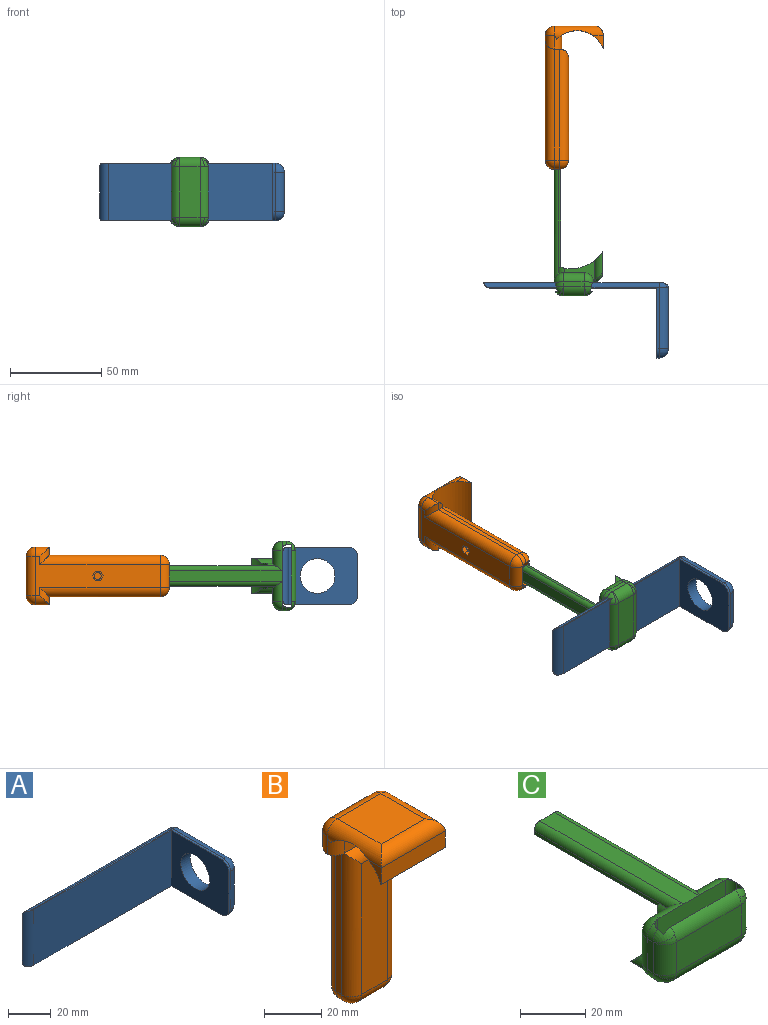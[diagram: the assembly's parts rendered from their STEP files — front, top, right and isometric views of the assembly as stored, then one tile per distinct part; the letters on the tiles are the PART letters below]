
ASSEMBLY  parts=3 mates=2
PART A: 23 faces, bbox 101.6x41.6x32.6 mm
  f0: cylinder r=3.17mm len=24.95mm, axis (0,0,1), area 116.1mm2, adj f1,f5,f12,f14
  f1: plane 98.43x26.67mm, normal (0,1,0), area 2624mm2, adj f0,f9,f10,f13,f16,f22
  f2: plane 94.27x33.66mm, normal (0,0,1), area 101.3mm2, adj f6,f7,f10,f15,f17,f22
  f3: plane 94.27x33.66mm, normal (0,0,-1), area 101.3mm2, adj f6,f7,f9,f11,f21,f22
  f4: plane 21.59x1.27mm, normal (0,-1,0), area 27.4mm2, adj f7,f17,f19,f21
  f5: plane 33.02x21.59mm, normal (1,0,0), area 427.9mm2, adj f0,f8,f11,f15,f19
  f6: plane 90.54x31.75mm, normal (0,-1,0), area 2874.7mm2, adj f2,f3,f7,f22
  f7: plane 38.1x31.75mm, normal (-1,0,0), area 913.6mm2, adj f2,f3,f4,f6,f8,f17,f21
  f8: cylinder r=9.53mm len=19.05mm, axis (1,0,0), area 380mm2, adj f5,f7
  f9: cylinder r=2.54mm len=96.52mm, axis (-1,0,0), area 382.7mm2, adj f1,f3,f13,f22
  f10: cylinder r=2.54mm len=96.52mm, axis (-1,0,0), area 382.7mm2, adj f1,f2,f16,f22
  f11: cylinder r=5.08mm len=33.66mm, axis (0,1,0), area 267.4mm2, adj f3,f5,f12,f13,f20
  f12: bspline ~4x3.91mm, area 8.6mm2, adj f0,f11,f13
  f13: torus R=2.54mm, axis (0,-1,0), area 14.1mm2, adj f1,f9,f11,f12
  f14: bspline ~4x3.91mm, area 8.6mm2, adj f0,f15,f16
  f15: cylinder r=5.08mm len=33.66mm, axis (0,-1,0), area 267.4mm2, adj f2,f5,f14,f16,f18
  f16: torus R=2.54mm, axis (0,-1,0), area 14.1mm2, adj f1,f10,f14,f15
  f17: cylinder r=5.08mm len=5.08mm, axis (-1,0,0), area 10.1mm2, adj f2,f4,f7,f18
  f18: sphere r=5.08mm, area 40.5mm2, adj f15,f17,f19
  f19: cylinder r=5.08mm len=21.59mm, axis (0,0,-1), area 172.3mm2, adj f4,f5,f18,f20
  f20: sphere r=5.08mm, area 40.5mm2, adj f11,f19,f21
  f21: cylinder r=5.08mm len=5.08mm, axis (1,0,0), area 10.1mm2, adj f3,f4,f7,f20
  f22: cylinder r=5.08mm len=31.75mm, axis (0,0,1), area 188.1mm2, adj f1,f2,f3,f6,f9,f10
PART B: 53 faces, bbox 32.4x32.5x79.4 mm
  f0: plane 7.11x5.98mm, normal (-1,0,0), area 17.6mm2, adj f14,f15,f17,f37
  f1: plane 7.11x5.98mm, normal (1,0,0), area 17.6mm2, adj f14,f15,f17,f40
  f2: plane 68.58x21.59mm, normal (0,1,0), area 874.6mm2, adj f20,f21,f22,f23,f24,f25,f28,f29
  f3: plane 60.96x2.59mm, normal (-1,0,0), area 157.9mm2, adj f18,f29,f31,f47
  f4: plane 56.04x12.75mm, normal (0,-1,0), area 714.6mm2, adj f30,f31,f32,f43
  f5: cylinder r=2.54mm len=63.49mm, axis (0,0,-1), area 253.1mm2, adj f6,f10,f12,f47,f49,f50
  f6: plane 63.46x10.16mm, normal (0,-1,0), area 633.4mm2, adj f5,f7,f12,f27,f50
  f7: cylinder r=2.54mm len=63.49mm, axis (0,0,-1), area 253.1mm2, adj f6,f8,f12,f46,f48,f50
  f8: plane 63.35x2.54mm, normal (-1,0,0), area 160.7mm2, adj f7,f9,f12,f44,f46
  f9: plane 63.38x15.47mm, normal (0,1,0), area 962.3mm2, adj f8,f10,f12,f43,f44,f45
  f10: plane 64x3.2mm, normal (1,0,0), area 160.7mm2, adj f5,f9,f12,f45,f47
  f11: plane 60.96x2.59mm, normal (1,0,0), area 157.9mm2, adj f19,f28,f32,f46
  f12: plane 15.24x5.08mm, normal (0,0,-1), area 74.7mm2, adj f5,f6,f7,f8,f9,f10
  f13: plane 21.69x21.59mm, normal (0,0,1), area 468.3mm2, adj f35,f37,f39,f40
  f14: plane 31.75x7.11mm, normal (0,-1,0), area 225.8mm2, adj f0,f1,f17,f39
  f15: cylinder r=15.35mm len=31.75mm, axis (-1,0,0), area 866.3mm2, adj f0,f1,f16,f17,f37,f40,f41,f42
  f16: plane 21.89x7.62mm, normal (0,-1,0), area 166.8mm2, adj f15,f30,f41,f42
  f17: plane 31.75x0.19mm, normal (0,0,-1), area 6.1mm2, adj f0,f1,f14,f15
  f18: plane 4.58x3.85mm, normal (0,0,-1), area 12.2mm2, adj f3,f31,f42,f51
  f19: plane 4.58x3.85mm, normal (0,0,-1), area 12.2mm2, adj f11,f32,f41,f52
  f20: plane 2.93x2.54mm, normal (1,0,0), area 7.4mm2, adj f2,f21,f25,f26
  f21: plane 2.54x2.54mm, normal (0.5,0,-0.87), area 7.4mm2, adj f2,f20,f22,f26
  f22: plane 2.54x2.54mm, normal (-0.5,0,-0.87), area 7.4mm2, adj f2,f21,f23,f26
  f23: plane 2.93x2.54mm, normal (-1,0,0), area 7.4mm2, adj f2,f22,f24,f26
  f24: plane 2.54x2.54mm, normal (-0.5,0,0.87), area 7.4mm2, adj f2,f23,f25,f26
  f25: plane 2.54x2.54mm, normal (0.5,0,0.87), area 7.4mm2, adj f2,f20,f24,f26
  f26: plane 5.87x5.08mm, normal (0,1,0), area 10.9mm2, adj f20,f21,f22,f23,f24,f25,f27
  f27: cylinder r=1.91mm len=3.81mm, axis (0,1,0), area 22.8mm2, adj f6,f26
  f28: cylinder r=5.08mm len=66.04mm, axis (0,0,-1), area 501.2mm2, adj f2,f11,f48,f52
  f29: cylinder r=5.08mm len=66.04mm, axis (0,0,-1), area 501.2mm2, adj f2,f3,f49,f51
  f30: cylinder r=5.08mm len=22.59mm, axis (-1,0,0), area 124.1mm2, adj f4,f16,f31,f32,f41,f42
  f31: cylinder r=5.08mm len=60.96mm, axis (0,0,-1), area 472.9mm2, adj f3,f4,f18,f30,f42,f45
  f32: cylinder r=5.08mm len=60.96mm, axis (0,0,-1), area 472.9mm2, adj f4,f11,f19,f30,f41,f44
  f33: cylinder r=5.08mm len=7.62mm, axis (0,0,-1), area 46.1mm2, adj f2,f34,f42,f51
  f34: sphere r=5.08mm, area 40.5mm2, adj f33,f35,f37
  f35: cylinder r=5.08mm len=21.59mm, axis (-1,0,0), area 172.3mm2, adj f2,f13,f34,f38
  f36: cylinder r=5.08mm len=7.62mm, axis (0,0,-1), area 46.1mm2, adj f2,f38,f41,f52
  f37: cylinder r=5.08mm len=26.77mm, axis (0,-1,0), area 172.8mm2, adj f0,f13,f15,f34,f39,f42
  f38: sphere r=5.08mm, area 40.5mm2, adj f35,f36,f40
  f39: cylinder r=5.08mm len=31.75mm, axis (-1,0,0), area 223.9mm2, adj f13,f14,f37,f40
  f40: cylinder r=5.08mm len=26.77mm, axis (0,-1,0), area 172.8mm2, adj f1,f13,f15,f38,f39,f41
  f41: cylinder r=5.08mm len=7.62mm, axis (0,0,-1), area 45.9mm2, adj f15,f16,f19,f30,f32,f36,f40
  f42: cylinder r=5.08mm len=7.62mm, axis (0,0,-1), area 45.9mm2, adj f15,f16,f18,f30,f31,f33,f37
  f43: cylinder r=5.08mm len=12.75mm, axis (1,0,0), area 77.5mm2, adj f4,f9,f44,f45
  f44: sphere r=5.08mm, area 38.1mm2, adj f8,f9,f32,f43,f46
  f45: sphere r=5.08mm, area 37.7mm2, adj f9,f10,f31,f43,f47
  f46: cylinder r=5.08mm len=5.07mm, axis (0,-1,0), area 18.2mm2, adj f7,f8,f11,f44,f48
  f47: cylinder r=5.08mm len=5.07mm, axis (0,-1,0), area 18.2mm2, adj f3,f5,f10,f45,f49
  f48: sphere r=5.08mm, area 40.4mm2, adj f7,f28,f46,f50
  f49: sphere r=5.08mm, area 40.4mm2, adj f5,f29,f47,f50
  f50: cylinder r=5.08mm len=12.75mm, axis (1,0,0), area 94.1mm2, adj f2,f5,f6,f7,f48,f49
  f51: cylinder r=5.08mm len=9.5mm, axis (-1,0,0), area 35.3mm2, adj f2,f18,f29,f33
  f52: cylinder r=5.08mm len=9.5mm, axis (-1,0,0), area 35.3mm2, adj f2,f19,f28,f36
PART C: 76 faces, bbox 38.2x70x26.8 mm
  f0: plane 16.33x11.11mm, normal (-1,0,0), area 63.2mm2, adj f1,f2,f9,f66,f69,f73,f74
  f1: cylinder r=13.73mm len=13.97mm, axis (1,0,0), area 54.9mm2, adj f0,f26,f48,f49,f50,f66,f74,f75
  f2: plane 11.43x7.05mm, normal (0,1,0), area 57.1mm2, adj f0,f9,f10,f42,f51,f55,f56,f74
  f3: plane 11.43x7.05mm, normal (0,1,0), area 57.1mm2, adj f6,f7,f12,f49,f61,f62,f63,f75
  f4: cylinder r=2.54mm len=5.08mm, axis (0,1,0), area 40.5mm2, adj f21,f57
  f5: cylinder r=2.54mm len=5.08mm, axis (0,1,0), area 40.5mm2, adj f21,f64
  f6: cylinder r=5.08mm len=11.43mm, axis (0,0,-1), area 88.4mm2, adj f3,f8,f18,f36,f58,f63
  f7: cylinder r=5.08mm len=9.53mm, axis (1,0,0), area 40.3mm2, adj f3,f8,f21,f49,f59,f60,f61,f71
  f8: sphere r=5.08mm, area 38.9mm2, adj f6,f7,f21,f37,f58,f59
  f9: cylinder r=5.08mm len=9.53mm, axis (1,0,0), area 40.3mm2, adj f0,f2,f11,f21,f51,f52,f53,f73
  f10: cylinder r=5.08mm len=11.43mm, axis (0,0,1), area 88.4mm2, adj f2,f11,f17,f44,f54,f55
  f11: sphere r=5.08mm, area 38.9mm2, adj f9,f10,f21,f45,f53,f54
  f12: cylinder r=5.08mm len=10.8mm, axis (1,0,0), area 69mm2, adj f3,f21,f27,f36,f75
  f13: plane 54.1x1.27mm, normal (1,0,0), area 68.7mm2, adj f16,f26,f27,f48
  f14: plane 62.23x6.35mm, normal (0,0,1), area 395.2mm2, adj f16,f21,f27,f28
  f15: plane 54.1x1.27mm, normal (-1,0,0), area 68.7mm2, adj f16,f26,f28,f50
  f16: plane 11.43x3.81mm, normal (0,1,0), area 40.8mm2, adj f13,f14,f15,f26,f27,f28
  f17: plane 11.43x2.54mm, normal (-1,0,0), area 29mm2, adj f10,f31,f43,f45
  f18: plane 11.43x2.54mm, normal (1,0,0), area 29mm2, adj f6,f30,f35,f37
  f19: plane 19.36x2.54mm, normal (-1,0,0), area 47.7mm2, adj f20,f24,f34,f39
  f20: cylinder r=2.54mm len=21.51mm, axis (0,0,1), area 81.3mm2, adj f19,f21,f35,f37
  f21: plane 29.21x21.59mm, normal (0,-1,0), area 590.1mm2, adj f4,f5,f7,f8,f9,f11,f12,f14
  f22: cylinder r=2.54mm len=21.51mm, axis (0,0,1), area 81.3mm2, adj f21,f23,f43,f45
  f23: plane 19.36x2.54mm, normal (1,0,0), area 47.7mm2, adj f22,f24,f41,f46
  f24: plane 34.29x20.23mm, normal (0,1,0), area 688.3mm2, adj f19,f23,f29,f32,f34,f39,f41,f46
  f25: plane 27.94x11.43mm, normal (0,-1,0), area 319.4mm2, adj f29,f30,f31,f32
  f26: plane 54.1x11.43mm, normal (0,0,-1), area 618.3mm2, adj f1,f13,f15,f16
  f27: cylinder r=2.54mm len=62.23mm, axis (0,1,0), area 238.3mm2, adj f12,f13,f14,f16,f75
  f28: cylinder r=2.54mm len=62.23mm, axis (0,1,0), area 238.3mm2, adj f14,f15,f16,f42,f74
  f29: cylinder r=5.08mm len=27.94mm, axis (-1,0,0), area 148.6mm2, adj f24,f25,f33,f34,f40,f41
  f30: cylinder r=5.08mm len=11.43mm, axis (0,0,-1), area 91.2mm2, adj f18,f25,f33,f38
  f31: cylinder r=5.08mm len=11.43mm, axis (0,0,-1), area 91.2mm2, adj f17,f25,f40,f47
  f32: cylinder r=5.08mm len=27.94mm, axis (-1,0,0), area 148.6mm2, adj f24,f25,f38,f39,f46,f47
  f33: sphere r=5.08mm, area 10.4mm2, adj f29,f30,f34
  f34: sphere r=5.08mm, area 20.9mm2, adj f19,f24,f29,f33,f35
  f35: cylinder r=5.08mm len=5.04mm, axis (0,-1,0), area 13.2mm2, adj f18,f20,f34,f36
  f36: sphere r=5.08mm, area 40.5mm2, adj f6,f12,f21,f35
  f37: cylinder r=5.08mm len=5.04mm, axis (0,-1,0), area 13.2mm2, adj f8,f18,f20,f39
  f38: sphere r=5.08mm, area 10.4mm2, adj f30,f32,f39
  f39: sphere r=5.08mm, area 20.9mm2, adj f19,f24,f32,f37,f38
  f40: sphere r=5.08mm, area 10.4mm2, adj f29,f31,f41
  f41: sphere r=5.08mm, area 20.9mm2, adj f23,f24,f29,f40,f43
  f42: cylinder r=5.08mm len=10.8mm, axis (1,0,0), area 69mm2, adj f2,f21,f28,f44,f74
  f43: cylinder r=5.08mm len=5.04mm, axis (0,1,0), area 13.2mm2, adj f17,f22,f41,f44
  f44: sphere r=5.08mm, area 40.5mm2, adj f10,f21,f42,f43
  f45: cylinder r=5.08mm len=5.04mm, axis (0,1,0), area 13.2mm2, adj f11,f17,f22,f46
  f46: sphere r=5.08mm, area 20.9mm2, adj f23,f24,f32,f45,f47
  f47: sphere r=5.08mm, area 10.4mm2, adj f31,f32,f46
  f48: plane 1.27x0.82mm, normal (0,1,0), area 0.6mm2, adj f1,f13,f75
  f49: plane 16.33x11.11mm, normal (1,0,0), area 63.2mm2, adj f1,f3,f7,f66,f70,f71,f75
  f50: plane 1.27x0.82mm, normal (0,1,0), area 0.6mm2, adj f1,f15,f74
  f51: plane 4.03x2.54mm, normal (-1,0,0), area 10.2mm2, adj f2,f9,f52,f56,f57
  f52: plane 3.49x2.35mm, normal (-0.5,0,0.87), area 7.6mm2, adj f9,f51,f53,f57
  f53: plane 3.63x2.39mm, normal (0.5,0,0.87), area 7.6mm2, adj f9,f11,f52,f54,f57
  f54: plane 4.05x2.47mm, normal (1,0,0), area 9.8mm2, adj f10,f11,f53,f55,f57
  f55: plane 3.5x2.54mm, normal (0.5,0,-0.87), area 10.2mm2, adj f2,f10,f54,f56,f57
  f56: plane 3.49x2.54mm, normal (-0.5,0,-0.87), area 10.2mm2, adj f2,f51,f55,f57
  f57: plane 8.07x6.99mm, normal (0,1,0), area 22mm2, adj f4,f51,f52,f53,f54,f55,f56
  f58: plane 4.05x2.47mm, normal (-1,0,0), area 9.8mm2, adj f6,f8,f59,f63,f64
  f59: plane 3.63x2.39mm, normal (-0.5,0,0.87), area 7.6mm2, adj f7,f8,f58,f60,f64
  f60: plane 3.49x2.35mm, normal (0.5,0,0.87), area 7.6mm2, adj f7,f59,f61,f64
  f61: plane 4.03x2.54mm, normal (1,0,0), area 10.2mm2, adj f3,f7,f60,f62,f64
  f62: plane 3.49x2.54mm, normal (0.5,0,-0.87), area 10.2mm2, adj f3,f61,f63,f64
  f63: plane 3.5x2.54mm, normal (-0.5,0,-0.87), area 10.2mm2, adj f3,f6,f58,f62,f64
  f64: plane 8.07x6.99mm, normal (0,1,0), area 22mm2, adj f5,f58,f59,f60,f61,f62,f63
  f65: plane 19.05x11.68mm, normal (0,0,-1), area 222.6mm2, adj f66,f67,f68,f72
  f66: cylinder r=20.32mm len=19.05mm, axis (1,0,0), area 336mm2, adj f0,f1,f49,f65,f67,f68,f69,f70
  f67: plane 11.68x0.05mm, normal (1,0,0), area 0.5mm2, adj f65,f66,f70,f71
  f68: plane 11.68x0.05mm, normal (-1,0,0), area 0.5mm2, adj f65,f66,f69,f73
  f69: cylinder r=5.08mm len=16.01mm, axis (0,1,0), area 58.9mm2, adj f0,f66,f68,f73
  f70: cylinder r=5.08mm len=16.01mm, axis (0,1,0), area 58.9mm2, adj f49,f66,f67,f71
  f71: cylinder r=5.08mm len=5.13mm, axis (0,0,-1), area 12mm2, adj f7,f49,f67,f70,f72
  f72: cylinder r=5.08mm len=19.05mm, axis (1,0,0), area 122.6mm2, adj f21,f65,f71,f73
  f73: cylinder r=5.08mm len=5.13mm, axis (0,0,-1), area 12mm2, adj f0,f9,f68,f69,f72
  f74: cylinder r=5.08mm len=3.73mm, axis (0,1,0), area 11.3mm2, adj f0,f1,f2,f28,f42,f50
  f75: cylinder r=5.08mm len=3.73mm, axis (0,1,0), area 11.3mm2, adj f1,f3,f12,f27,f48,f49
PLACE A t=(8.66,28.79,84.31)mm
PLACE B rot(axis=(-0.58,0.58,0.58),120deg) t=(3.3,70.76,100.19)mm
PLACE C rot(axis=(0,-1,0),90deg) t=(22.67,14.59,121.9)mm
MATE slider A.f1 <-> C.f21  axis (0,1,0) through (14.07,8.47,100.19)mm
MATE slider C.f26 <-> B.f9  axis (1,0,0) through (7.43,71.11,100.19)mm
